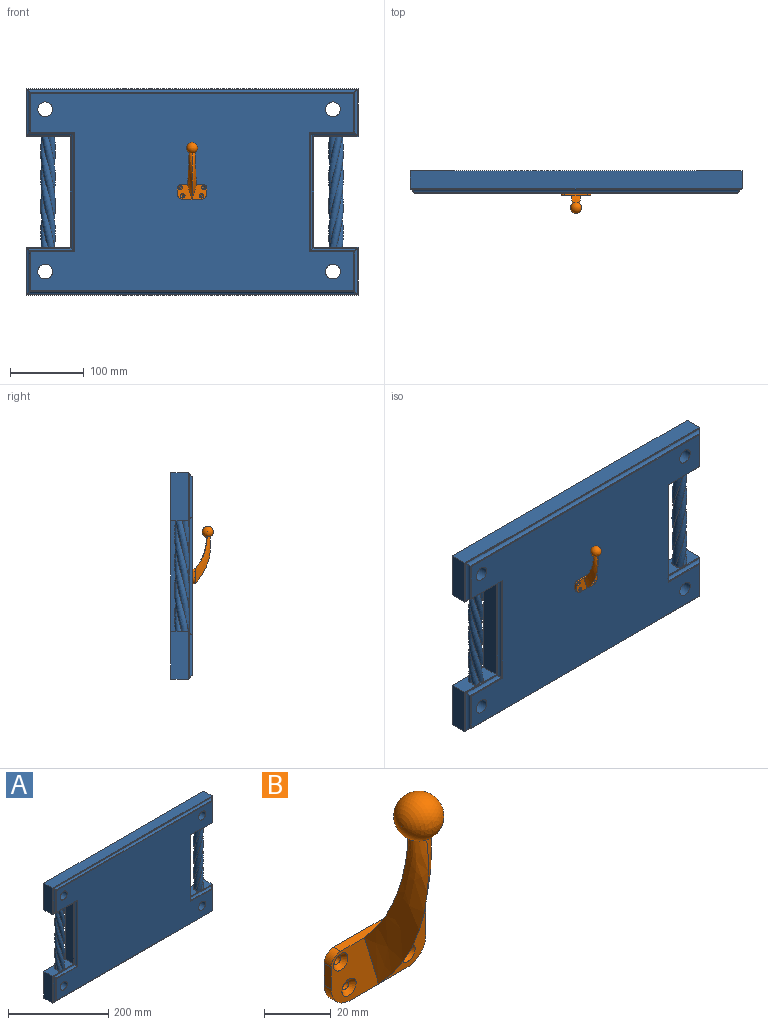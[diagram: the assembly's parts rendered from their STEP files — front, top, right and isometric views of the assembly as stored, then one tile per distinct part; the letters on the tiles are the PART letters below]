
ASSEMBLY  parts=2 mates=1
PART A: 64 faces, bbox 450x32.1x280 mm
  f0: bspline ~150x32.05mm, area 2381.9mm2, adj f1,f3,f13,f18
  f1: bspline ~150x32.05mm, area 2381.9mm2, adj f0,f2,f13,f18
  f2: bspline ~150x32.05mm, area 2381.9mm2, adj f1,f3,f13,f18
  f3: bspline ~150x32.05mm, area 2381.9mm2, adj f0,f2,f13,f18
  f4: plane 450x24mm, normal (0,0,-1), area 10800mm2, adj f5,f7,f21,f58
  f5: plane 65x24mm, normal (1,0,0), area 1560mm2, adj f4,f8,f21,f58
  f6: plane 65x24mm, normal (1,0,0), area 1560mm2, adj f10,f11,f21,f58
  f7: plane 65x24mm, normal (-1,0,0), area 1560mm2, adj f4,f18,f21,f58
  f8: plane 60x24mm, normal (0,0,1), area 1182.9mm2, adj f5,f9,f21,f58,f60,f61,f62,f63
  f9: plane 150x24mm, normal (1,0,0), area 3600mm2, adj f8,f10,f21,f58
  f10: plane 60x24mm, normal (0,0,-1), area 1182.9mm2, adj f6,f9,f21,f58,f60,f61,f62,f63
  f11: plane 450x24mm, normal (0,0,1), area 10800mm2, adj f6,f12,f21,f58
  f12: plane 65x24mm, normal (-1,0,0), area 1560mm2, adj f11,f13,f21,f58
  f13: plane 60x24mm, normal (0,0,-1), area 1182.9mm2, adj f0,f1,f2,f3,f12,f14,f21,f58
  f14: plane 150x24mm, normal (-1,0,0), area 3600mm2, adj f13,f18,f21,f58
  f15: cylinder r=10mm len=30mm, axis (0,1,0), area 1885mm2, adj f20,f21
  f16: cylinder r=10mm len=30mm, axis (0,1,0), area 1885mm2, adj f20,f21
  f17: cylinder r=10mm len=30mm, axis (0,1,0), area 1885mm2, adj f20,f21
  f18: plane 60x24mm, normal (0,0,1), area 1182.9mm2, adj f0,f1,f2,f3,f7,f14,f21,f58
  f19: cylinder r=10mm len=30mm, axis (0,1,0), area 1885mm2, adj f20,f21
  f20: plane 438x268mm, normal (0,-1,0), area 96687.4mm2, adj f15,f16,f17,f19,f23,f26,f29,f32
  f21: plane 450x280mm, normal (0,1,0), area 106743.4mm2, adj f4,f5,f6,f7,f8,f9,f10,f11
  f22: cylinder r=5mm len=448mm, axis (1,0,0), area 2589.2mm2, adj f24,f25,f28,f56
  f23: plane 438x1mm, normal (0,0,-1), area 438mm2, adj f20,f26,f29,f56
  f24: plane 448x1.1mm, normal (0,0,-1), area 493.3mm2, adj f22,f27,f30,f58
  f25: cylinder r=5mm len=63mm, axis (0,0,1), area 340.6mm2, adj f22,f27,f33,f56
  f26: plane 53x1mm, normal (1,0,0), area 53mm2, adj f20,f23,f32,f56
  f27: plane 63x1.1mm, normal (1,0,0), area 69.4mm2, adj f24,f25,f31,f58
  f28: cylinder r=5mm len=63mm, axis (0,0,-1), area 340.6mm2, adj f22,f30,f34,f56
  f29: plane 53x1mm, normal (-1,0,0), area 53mm2, adj f20,f23,f35,f56
  f30: plane 63x1.1mm, normal (-1,0,0), area 69.4mm2, adj f24,f28,f36,f58
  f31: plane 60x1.1mm, normal (0,0,1), area 66.1mm2, adj f27,f33,f37,f58
  f32: plane 60x1mm, normal (0,0,1), area 60mm2, adj f20,f26,f38,f56
  f33: cylinder r=5mm len=63.9mm, axis (-1,0,0), area 350.4mm2, adj f25,f31,f39,f56
  f34: cylinder r=5mm len=63.9mm, axis (-1,0,0), area 350.4mm2, adj f28,f36,f42,f56
  f35: plane 60x1mm, normal (0,0,1), area 60mm2, adj f20,f29,f41,f56
  f36: plane 60x1.1mm, normal (0,0,1), area 66.1mm2, adj f30,f34,f40,f58
  f37: plane 152x1.1mm, normal (1,0,0), area 167.4mm2, adj f31,f39,f45,f58
  f38: plane 162x1mm, normal (1,0,0), area 162mm2, adj f20,f32,f44,f56
  f39: cylinder r=5mm len=159.8mm, axis (0,0,1), area 915.1mm2, adj f33,f37,f43,f56
  f40: plane 152x1.1mm, normal (-1,0,0), area 167.4mm2, adj f36,f42,f46,f58
  f41: plane 162x1mm, normal (-1,0,0), area 162mm2, adj f20,f35,f47,f56
  f42: cylinder r=5mm len=159.8mm, axis (0,0,-1), area 915.1mm2, adj f34,f40,f48,f56
  f43: cylinder r=5mm len=63.9mm, axis (1,0,0), area 350.4mm2, adj f39,f45,f49,f56
  f44: plane 60x1mm, normal (0,0,-1), area 60mm2, adj f20,f38,f50,f56
  f45: plane 60x1.1mm, normal (0,0,-1), area 66.1mm2, adj f37,f43,f51,f58
  f46: plane 60x1.1mm, normal (0,0,-1), area 66.1mm2, adj f40,f48,f54,f58
  f47: plane 60x1mm, normal (0,0,-1), area 60mm2, adj f20,f41,f53,f56
  f48: cylinder r=5mm len=63.9mm, axis (1,0,0), area 350.4mm2, adj f42,f46,f52,f56
  f49: cylinder r=5mm len=63mm, axis (0,0,1), area 340.6mm2, adj f43,f51,f55,f56
  f50: plane 53x1mm, normal (1,0,0), area 53mm2, adj f20,f44,f56,f57
  f51: plane 63x1.1mm, normal (1,0,0), area 69.4mm2, adj f45,f49,f58,f59
  f52: cylinder r=5mm len=63mm, axis (0,0,-1), area 340.6mm2, adj f48,f54,f55,f56
  f53: plane 53x1mm, normal (-1,0,0), area 53mm2, adj f20,f47,f56,f57
  f54: plane 63x1.1mm, normal (-1,0,0), area 69.4mm2, adj f46,f52,f58,f59
  f55: cylinder r=5mm len=448mm, axis (-1,0,0), area 2589.2mm2, adj f49,f52,f56,f59
  f56: plane 440.2x270.2mm, normal (0,-1,0), area 1823.7mm2, adj f22,f23,f25,f26,f28,f29,f32,f33
  f57: plane 438x1mm, normal (0,0,1), area 438mm2, adj f20,f50,f53,f56
  f58: plane 450x280mm, normal (0,-1,0), area 1696mm2, adj f4,f5,f6,f7,f8,f9,f10,f11
  f59: plane 448x1.1mm, normal (0,0,1), area 493.3mm2, adj f51,f54,f55,f58
  f60: bspline ~150x32.05mm, area 2381.9mm2, adj f8,f10,f61,f63
  f61: bspline ~150x32.05mm, area 2381.9mm2, adj f8,f10,f60,f62
  f62: bspline ~150x32.05mm, area 2381.9mm2, adj f8,f10,f61,f63
  f63: bspline ~150x32.05mm, area 2381.9mm2, adj f8,f10,f60,f62
PART B: 23 faces, bbox 40x27.5x77.5 mm
  f0: plane 20x20mm, normal (0,-1,0), area 266.3mm2, adj f2,f3,f4,f8,f9,f16,f17,f19
  f1: plane 8x3mm, normal (-1,0,0), area 24mm2, adj f5,f6,f7,f10
  f2: plane 24x3mm, normal (0,0,-1), area 72mm2, adj f0,f5,f6,f7,f8
  f3: plane 8x3mm, normal (1,0,0), area 24mm2, adj f0,f5,f8,f9
  f4: plane 32x3mm, normal (0,0,1), area 96mm2, adj f0,f5,f6,f9,f10,f20
  f5: plane 40x20mm, normal (0,1,0), area 737.4mm2, adj f1,f2,f3,f4,f7,f8,f9,f10
  f6: plane 20x20mm, normal (0,-1,0), area 266.3mm2, adj f1,f2,f4,f7,f10,f15,f18,f21
  f7: cylinder r=8mm len=8mm, axis (0,1,0), area 37.7mm2, adj f1,f2,f5,f6
  f8: cylinder r=8mm len=8mm, axis (0,-1,0), area 37.7mm2, adj f0,f2,f3,f5
  f9: cylinder r=4mm len=4mm, axis (0,1,0), area 18.8mm2, adj f0,f3,f4,f5
  f10: cylinder r=4mm len=4mm, axis (0,-1,0), area 18.8mm2, adj f1,f4,f5,f6
  f11: cylinder r=1.5mm len=3mm, axis (0,-1,0), area 14.1mm2, adj f5,f15
  f12: cylinder r=1.5mm len=3mm, axis (0,-1,0), area 14.1mm2, adj f5,f18
  f13: cylinder r=1.5mm len=3mm, axis (0,-1,0), area 14.1mm2, adj f5,f17
  f14: cylinder r=1.5mm len=3mm, axis (0,-1,0), area 14.1mm2, adj f5,f16
  f15: cone r=1.5mm half-angle=45deg, axis (0,-1,0), area 30mm2, adj f6,f11
  f16: cone r=1.5mm half-angle=45deg, axis (0,-1,0), area 30mm2, adj f0,f14
  f17: cone r=1.5mm half-angle=45deg, axis (0,-1,0), area 30mm2, adj f0,f13
  f18: cone r=1.5mm half-angle=45deg, axis (0,-1,0), area 30mm2, adj f6,f12
  f19: bspline ~66.97x21.23mm, area 608.1mm2, adj f0,f20,f21,f22
  f20: bspline ~43.65x16.2mm, area 461.2mm2, adj f4,f19,f21,f22
  f21: bspline ~64.82x21.14mm, area 608.1mm2, adj f6,f19,f20,f22
  f22: sphere r=7.5mm, area 673.6mm2, adj f19,f20,f21
PLACE A t=(-7.89,15,14.2)mm fixed
PLACE B t=(-7.84,-18,13.97)mm
MATE revolute B.f5 <-> A.f20  axis (0,1,0) through (-7.84,-15,14.17)mm
